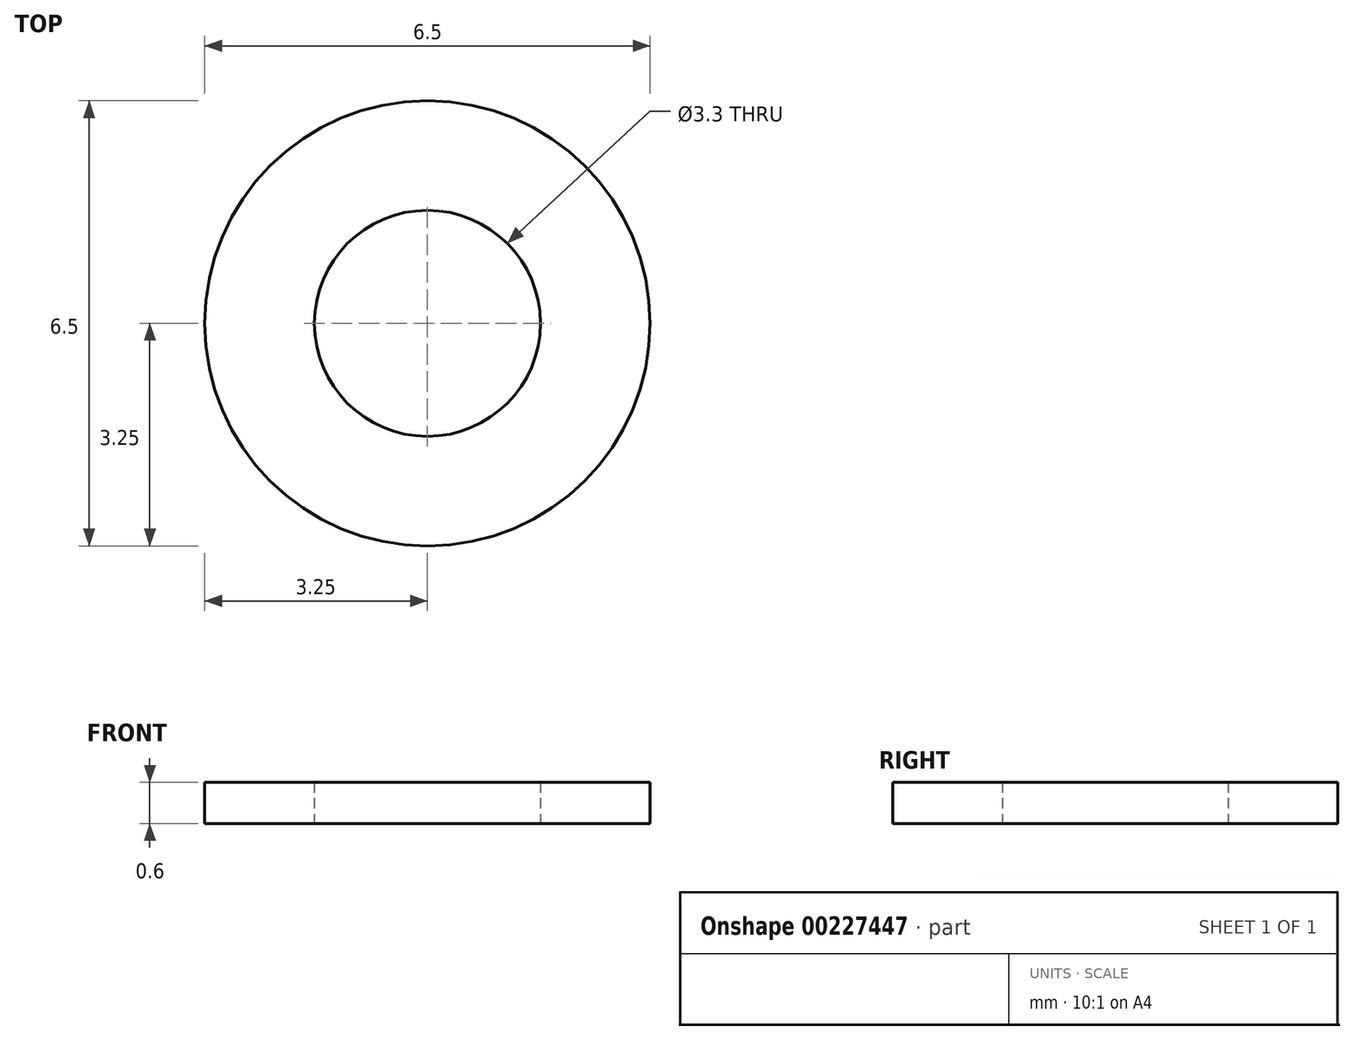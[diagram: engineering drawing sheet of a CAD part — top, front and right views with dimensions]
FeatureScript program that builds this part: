
annotation { "Feature Type Name" : "Feature", "Feature Type Description" : "" }
export const myFeature = defineFeature(function(context is Context, id is Id, definition is map)
    precondition{}
    {
        {
            var Q0;
            Q0=qCreatedBy(makeId("Top.planeOp"),FACE);
            var sketch = newSketch(context, id + "F0", { "sketchPlane" : qUnion([Q0])});
            skCircle(sketch, "E0", {"center": v(0, 0) * mm, "radius": 1.65 * mm});
            skCircle(sketch, "E1", {"center": v(0, 0) * mm, "radius": 3.25 * mm});
            skSolve(sketch);
        }
        {
            var Q0;
            Q0=makeQuery(id+"F0.imprint","IMPRINT",FACE,{"disambiguationData":[TD([[makeQuery(id+"F0.imprint","IMPRINT",EDGE,{"derivedFrom":sQuery(id+"F0.wireOp",EDGE,"E0")}),-1.0]])]});
            extrude(context, id + "F1", {"entities" : qUnion([Q0]), "depth" : 0.6 * mm});
        }
    });
